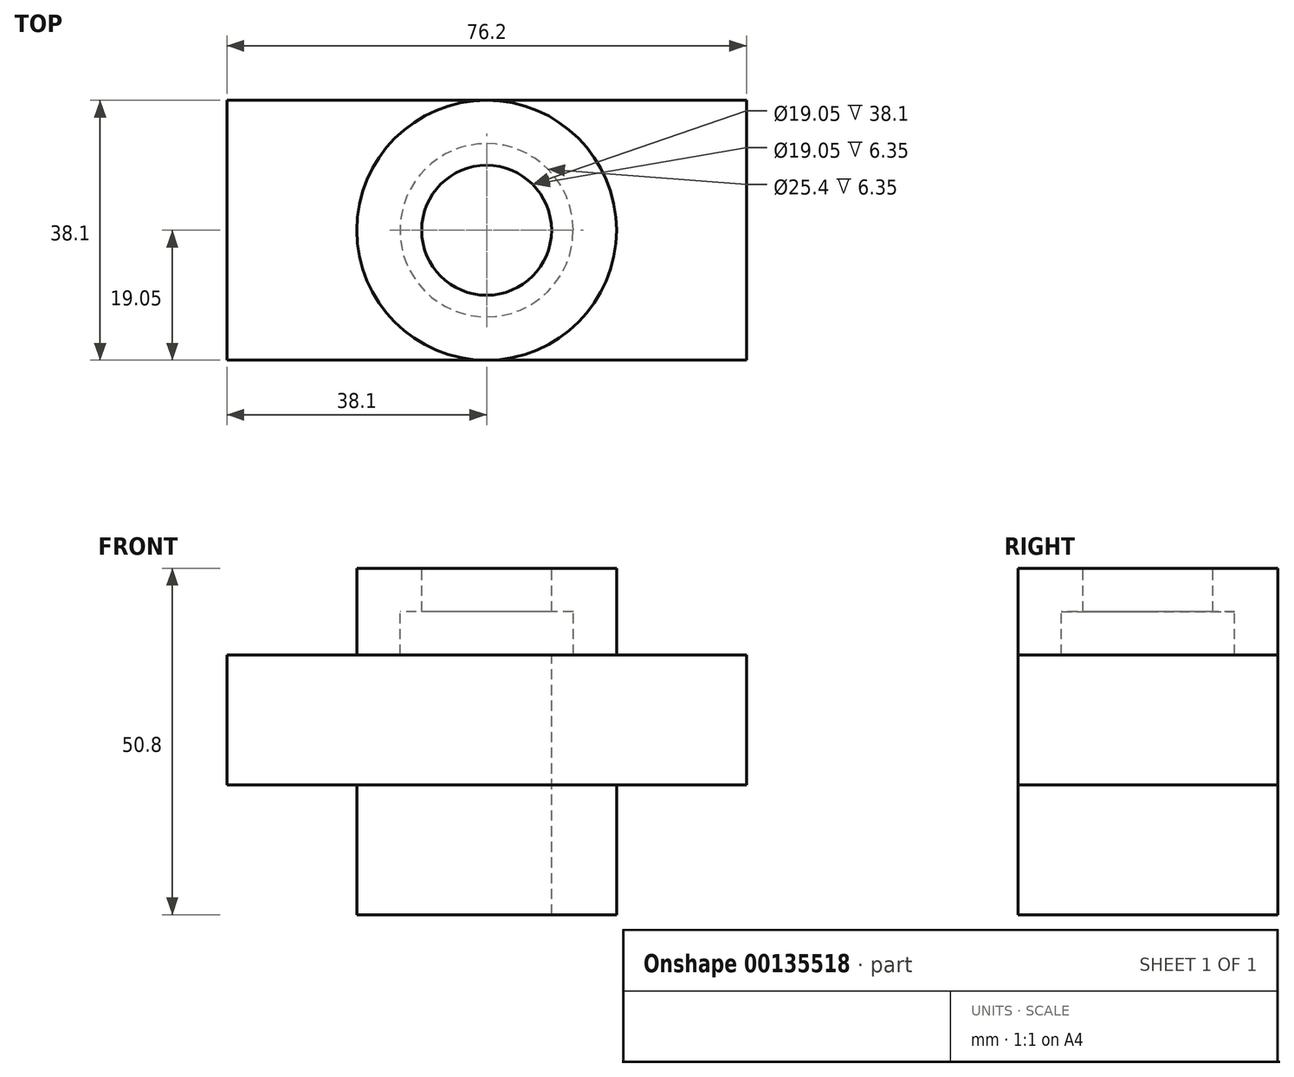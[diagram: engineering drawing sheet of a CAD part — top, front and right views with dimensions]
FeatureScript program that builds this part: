
annotation { "Feature Type Name" : "Feature", "Feature Type Description" : "" }
export const myFeature = defineFeature(function(context is Context, id is Id, definition is map)
    precondition{}
    {
        {
            var Q0;
            Q0=qCreatedBy(makeId("Front.planeOp"),FACE);
            var sketch = newSketch(context, id + "F0", { "sketchPlane" : qUnion([Q0])});
            skLineSegment(sketch, "E0", {"start": v(0, 0) * mm, "end": v(9.53, 0) * mm, "construction": true});
            skLineSegment(sketch, "E1", {"start": v(9.53, 0) * mm, "end": v(9.53, 12.7) * mm});
            skLineSegment(sketch, "E2", {"start": v(9.52, 12.7) * mm, "end": v(12.7, 12.7) * mm});
            skLineSegment(sketch, "E3", {"start": v(12.7, 12.7) * mm, "end": v(12.7, 19.05) * mm});
            skLineSegment(sketch, "E4", {"start": v(12.7, 19.05) * mm, "end": v(9.52, 19.05) * mm});
            skLineSegment(sketch, "E5", {"start": v(9.52, 19.05) * mm, "end": v(9.52, 25.4) * mm});
            skLineSegment(sketch, "E6", {"start": v(9.52, 25.4) * mm, "end": v(19.05, 25.4) * mm});
            skLineSegment(sketch, "E7", {"start": v(19.05, 25.4) * mm, "end": v(19.05, -25.4) * mm});
            skLineSegment(sketch, "E8", {"start": v(9.53, 0) * mm, "end": v(9.53, -25.4) * mm});
            skLineSegment(sketch, "E9", {"start": v(9.53, -25.4) * mm, "end": v(19.05, -25.4) * mm});
            skLineSegment(sketch, "E10", {"start": v(0, 0) * mm, "end": v(0, -10.35) * mm, "construction": true});
            skSolve(sketch);
        }
        {
            var Q0;
            Q0 = qSketchRegion(id + "F0", true);
            var Q1;
            Q1=sQuery(id+"F0.wireOp",EDGE,"E10");
            revolve(context, id + "F1", {"entities" : qUnion([Q0]), "axis" : qUnion([Q1]), "revolveType" : RevolveType.FULL});
        }
        {
            var Q0;
            Q0=qCreatedBy(makeId("Top.planeOp"),FACE);
            var sketch = newSketch(context, id + "F2", { "sketchPlane" : qUnion([Q0])});
            skLineSegment(sketch, "E11.bottom", {"start": v(38.1, 19.05) * mm, "end": v(-38.1, 19.05) * mm});
            skLineSegment(sketch, "E11.top", {"start": v(38.1, -19.05) * mm, "end": v(-38.1, -19.05) * mm});
            skLineSegment(sketch, "E11.left", {"start": v(38.1, 19.05) * mm, "end": v(38.1, -19.05) * mm});
            skLineSegment(sketch, "E11.right", {"start": v(-38.1, 19.05) * mm, "end": v(-38.1, -19.05) * mm});
            skPoint(sketch, "E11.middle", {"position": v(0, 0) * mm});
            skCircle(sketch, "E12", {"center": v(0, 0) * mm, "radius": 19.05 * mm});
            skSolve(sketch);
        }
        {
            var Q0;
            Q0=makeQuery(id+"F2.imprint","IMPRINT",FACE,{"disambiguationData":[TD([[makeQuery(id+"F2.imprint","IMPRINT",EDGE,{"derivedFrom":sQuery(id+"F2.wireOp",EDGE,"E11.bottom")}),1.0]])]});
            extrude(context, id + "F3", {"entities" : qUnion([Q0]), "operationType" : NewBodyOperationType.ADD, "endBound" : BoundingType.SYMMETRIC, "depth" : 12.7 * mm});
        }
        {
            var Q0;
            Q0=makeQuery(id+"F3.opExtrude","CAP_FACE",FACE,{"disambiguationData":[OSD([sQuery(id+"F2.wireOp",EDGE,"E11.bottom"),sQuery(id+"F2.wireOp",EDGE,"E11.top"),sQuery(id+"F2.wireOp",EDGE,"E11.right"),sQuery(id+"F2.wireOp",EDGE,"E12")])],"isStart":false});
            var Q1;
            Q1=makeQuery(id+"F3.opExtrude","CAP_FACE",FACE,{"disambiguationData":[OSD([sQuery(id+"F2.wireOp",EDGE,"E11.bottom"),sQuery(id+"F2.wireOp",EDGE,"E11.top"),sQuery(id+"F2.wireOp",EDGE,"E11.left"),sQuery(id+"F2.wireOp",EDGE,"E12")])],"isStart":false});
            extrude(context, id + "F4", {"entities" : qUnion([Q0, Q1]), "operationType" : NewBodyOperationType.ADD, "endBound" : BoundingType.SYMMETRIC, "depth" : 12.7 * mm});
        }
    });
